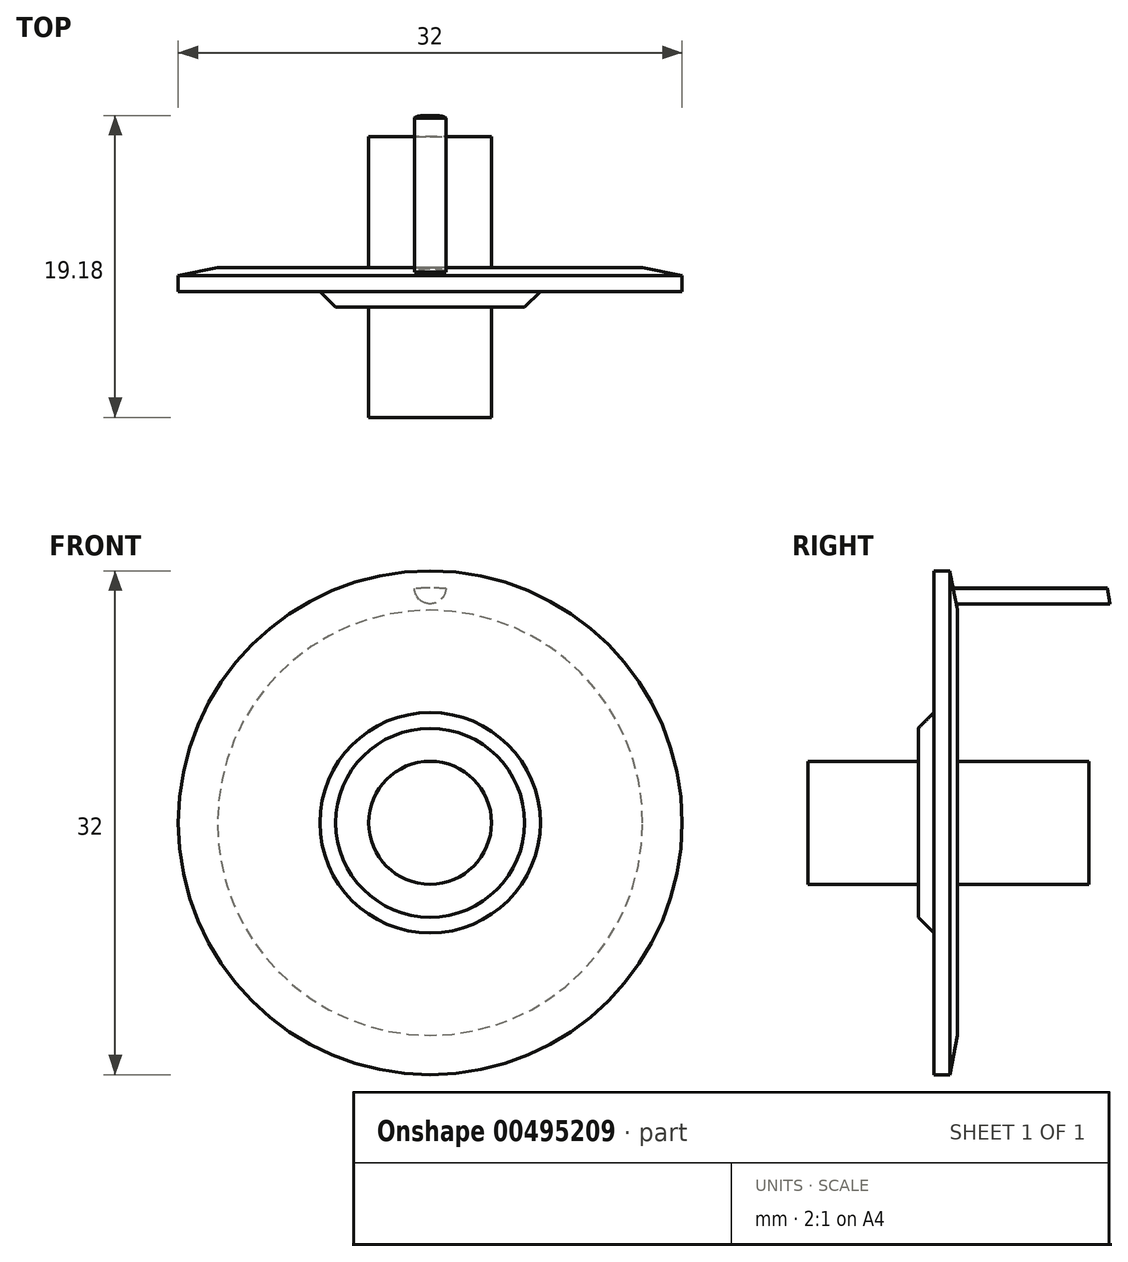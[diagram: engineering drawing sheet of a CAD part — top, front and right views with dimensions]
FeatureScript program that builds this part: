
annotation { "Feature Type Name" : "Feature", "Feature Type Description" : "" }
export const myFeature = defineFeature(function(context is Context, id is Id, definition is map)
    precondition{}
    {
        {
            var Q0;
            Q0=qCreatedBy(makeId("Front.planeOp"),FACE);
            var sketch = newSketch(context, id + "F0", { "sketchPlane" : qUnion([Q0])});
            skCircle(sketch, "E0", {"center": v(0, 0) * mm, "radius": 15.28 * mm});
            skCircle(sketch, "E1", {"center": v(0, 0) * mm, "radius": 14.9 * mm});
            skCircle(sketch, "E2", {"center": v(0, 14.9) * mm, "radius": 1 * mm});
            skCircle(sketch, "E3", {"center": v(0, 0) * mm, "radius": 3.9 * mm});
            skSolve(sketch);
        }
        {
            var Q0;
            {var subQ0=sQuery(id+"F0.wireOp",EDGE,"E2");var subQ1=sQuery(id+"F0.wireOp",EDGE,"E1");var subQ2=makeQuery(id+"F0.imprint","INTERSECT",VERTEX,{"disambiguationData":[OD(0.0)],"derivedFrom":[subQ1,subQ0]});Q0=makeQuery(id+"F0.imprint","IMPRINT",FACE,{"disambiguationData":[TD([[makeQuery(id+"F0.imprint","IMPRINT",EDGE,{"disambiguationData":[TD([[subQ2,-1.0]])],"derivedFrom":subQ1}),1.0]])]});}
            extrude(context, id + "F1", {"entities" : qUnion([Q0]), "depth" : 11 * mm});
        }
        {
            var Q0;
            {var subQ0=sQuery(id+"F0.wireOp",EDGE,"E2");var subQ1=sQuery(id+"F0.wireOp",EDGE,"E1");var subQ2=makeQuery(id+"F0.imprint","INTERSECT",VERTEX,{"disambiguationData":[OD(0.0)],"derivedFrom":[subQ1,subQ0]});Q0=makeQuery(id+"F0.imprint","IMPRINT",FACE,{"disambiguationData":[TD([[makeQuery(id+"F0.imprint","IMPRINT",EDGE,{"disambiguationData":[TD([[subQ2,1.0]])],"derivedFrom":subQ1}),1.0]])]});}
            extrude(context, id + "F2", {"entities" : qUnion([Q0]), "operationType" : NewBodyOperationType.REMOVE, "depth" : 11 * mm});
        }
        {
            var Q0;
            Q0=makeQuery(id+"F0.imprint","IMPRINT",FACE,{"disambiguationData":[TD([[makeQuery(id+"F0.imprint","IMPRINT",EDGE,{"derivedFrom":sQuery(id+"F0.wireOp",EDGE,"E3")}),1.0]])]});
            extrude(context, id + "F3", {"entities" : qUnion([Q0]), "operationType" : NewBodyOperationType.ADD, "depth" : (12.5 + 7) * mm});
        }
        {
            var Q0;
            Q0=qCreatedBy(makeId("Right.planeOp"),FACE);
            var sketch = newSketch(context, id + "F4", { "sketchPlane" : qUnion([Q0])});
            skLineSegment(sketch, "E4", {"start": v(0, 12) * mm, "end": v(0, 15) * mm});
            skLineSegment(sketch, "E5", {"start": v(0, 15) * mm, "end": v(-0.5, 15) * mm});
            skLineSegment(sketch, "E6", {"start": v(-0.5, 15) * mm, "end": v(0, 12) * mm});
            skLineSegment(sketch, "E7", {"start": v(-1.66, 0) * mm, "end": v(0, 0) * mm});
            skArc(sketch, "E8", {"start": v(0, 10) * mm, "mid": v(-1.23, 8.16) * mm, "end": v(-1.66, 6) * mm});
            skLineSegment(sketch, "E9", {"start": v(-1.66, 6) * mm, "end": v(-1.66, 0) * mm});
            skLineSegment(sketch, "E10", {"start": v(0, 0) * mm, "end": v(0, 10) * mm});
            skLineSegment(sketch, "E11.bottom", {"start": v(-10, 3.9) * mm, "end": v(-11.5, 3.9) * mm});
            skLineSegment(sketch, "E11.top", {"start": v(-10.5, 16) * mm, "end": v(-11.5, 16) * mm});
            skLineSegment(sketch, "E11.left", {"start": v(-10, 3.9) * mm, "end": v(-10, 13.5) * mm});
            skLineSegment(sketch, "E11.right", {"start": v(-11.5, 3.9) * mm, "end": v(-11.5, 16) * mm});
            skLineSegment(sketch, "E12", {"start": v(-10, 13.5) * mm, "end": v(-10.5, 16) * mm});
            skPoint(sketch, "E13.orphan", {"position": v(-10, 16) * mm});
            skLineSegment(sketch, "E14", {"start": v(-12.5, 3.9) * mm, "end": v(-12.5, 6) * mm});
            skLineSegment(sketch, "E15", {"start": v(-12.5, 6) * mm, "end": v(-11.5, 7) * mm});
            skLineSegment(sketch, "E16", {"start": v(-12.5, 3.9) * mm, "end": v(-11.5, 3.9) * mm});
            skSolve(sketch);
        }
        {
            var Q0;
            Q0=makeQuery(id+"F4.imprint","IMPRINT",FACE,{"disambiguationData":[TD([[makeQuery(id+"F4.imprint","IMPRINT",EDGE,{"derivedFrom":sQuery(id+"F4.wireOp",EDGE,"E4")}),1.0]])]});
            var Q1;
            Q1=makeQuery(id+"F4.imprint","IMPRINT",FACE,{"disambiguationData":[TD([[makeQuery(id+"F4.imprint","IMPRINT",EDGE,{"derivedFrom":sQuery(id+"F4.wireOp",EDGE,"E7")}),1.0]])]});
            var Q2;
            Q2=sQuery(id+"F0.wireOp",EDGE,"E0");
            revolve(context, id + "F5", {"operationType" : NewBodyOperationType.REMOVE, "entities" : qUnion([Q0, Q1]), "axis" : qUnion([Q2]), "revolveType" : RevolveType.FULL, "oppositeDirection" : true});
        }
        {
            var Q0;
            Q0=makeQuery(id+"F4.imprint","IMPRINT",FACE,{"disambiguationData":[TD([[makeQuery(id+"F4.imprint","IMPRINT",EDGE,{"derivedFrom":sQuery(id+"F4.wireOp",EDGE,"E11.bottom")}),-1.0]])]});
            var Q1;
            Q1=makeQuery(id+"F4.imprint","IMPRINT",FACE,{"disambiguationData":[TD([[makeQuery(id+"F4.imprint","IMPRINT",EDGE,{"derivedFrom":sQuery(id+"F4.wireOp",EDGE,"E14")}),-1.0]])]});
            var Q2;
            Q2=makeQuery(id+"F3.opExtrude","CAP_EDGE",EDGE,{"disambiguationData":[OSD([sQuery(id+"F0.wireOp",EDGE,"E3")])],"isStart":false});
            revolve(context, id + "F6", {"operationType" : NewBodyOperationType.ADD, "entities" : qUnion([Q0, Q1]), "axis" : qUnion([Q2]), "revolveType" : RevolveType.FULL});
        }
    });
